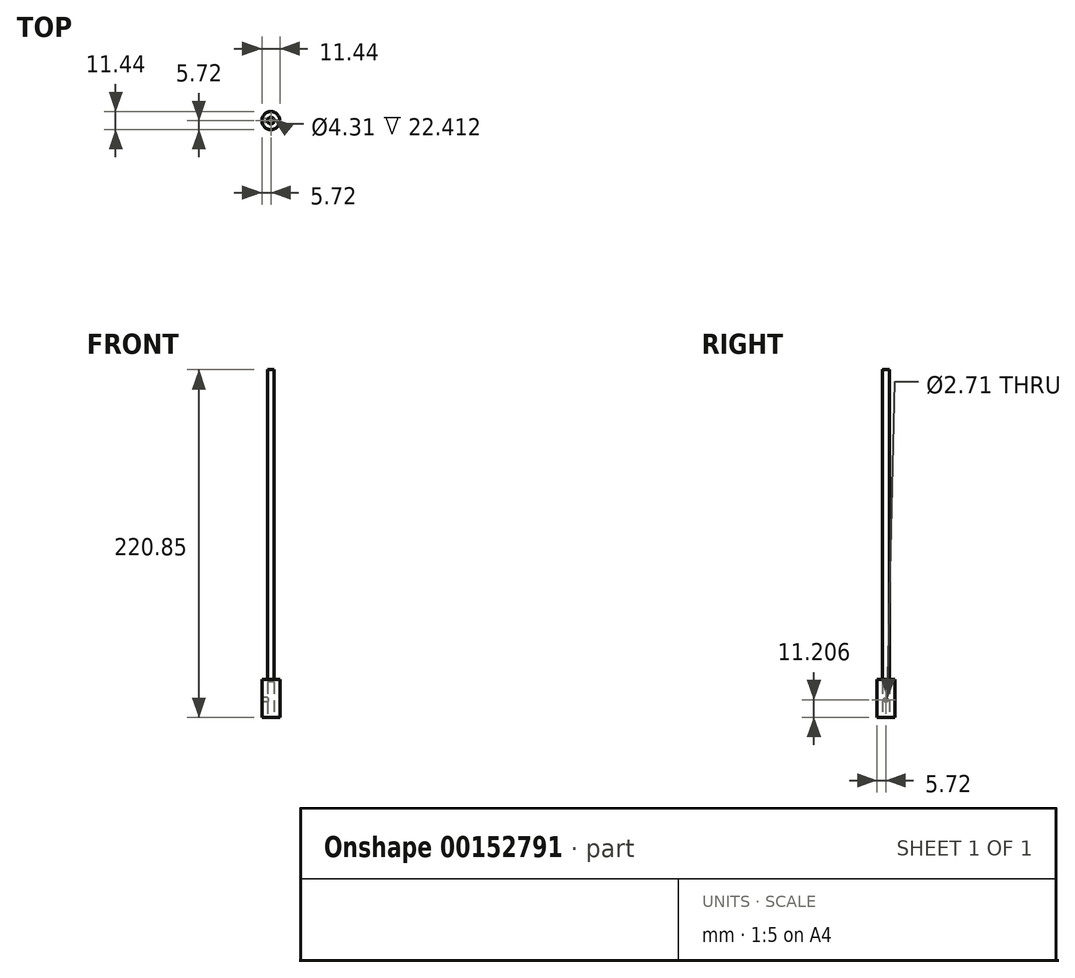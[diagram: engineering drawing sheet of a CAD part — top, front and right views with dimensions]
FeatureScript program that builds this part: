
annotation { "Feature Type Name" : "Feature", "Feature Type Description" : "" }
export const myFeature = defineFeature(function(context is Context, id is Id, definition is map)
    precondition{}
    {
        {
            var Q0;
            Q0=qCreatedBy(makeId("Top.planeOp"),FACE);
            var sketch = newSketch(context, id + "F0", { "sketchPlane" : qUnion([Q0])});
            skLineSegment(sketch, "E0.bottom", {"start": v(5.72, -5.72) * mm, "end": v(-5.72, -5.72) * mm});
            skLineSegment(sketch, "E0.top", {"start": v(5.72, 5.72) * mm, "end": v(-5.72, 5.71) * mm});
            skLineSegment(sketch, "E0.left", {"start": v(5.72, -5.72) * mm, "end": v(5.72, 5.72) * mm});
            skLineSegment(sketch, "E0.right", {"start": v(-5.72, -5.72) * mm, "end": v(-5.72, 5.71) * mm});
            skPoint(sketch, "E0.middle", {"position": v(0, 0) * mm});
            skCircle(sketch, "E1", {"center": v(0, 0) * mm, "radius": 5.72 * mm, "construction": true});
            skCircle(sketch, "E2", {"center": v(0, 0) * mm, "radius": 2.15 * mm});
            skLineSegment(sketch, "E3.bottom", {"start": v(2.15, 1.83) * mm, "end": v(5.41, 1.83) * mm, "construction": true});
            skLineSegment(sketch, "E3.top", {"start": v(2.15, -1.83) * mm, "end": v(5.41, -1.83) * mm, "construction": true});
            skLineSegment(sketch, "E3.left", {"start": v(2.15, 1.83) * mm, "end": v(2.15, -1.83) * mm, "construction": true});
            skLineSegment(sketch, "E3.right", {"start": v(5.41, 1.83) * mm, "end": v(5.41, -1.83) * mm, "construction": true});
            skLineSegment(sketch, "E4", {"start": v(2.15, 0) * mm, "end": v(0, 0) * mm, "construction": true});
            skSolve(sketch);
        }
        {
            var Q0;
            Q0=qSketchRegion(id+"F0",true);
            extrude(context, id + "F1", {"entities" : qUnion([Q0]), "depth" : 22.41 * mm});
        }
        {
            var Q0;
            Q0=makeQuery(id+"F1.opExtrude","CAP_FACE",FACE,{"disambiguationData":[OSD([sQuery(id+"F0.wireOp",EDGE,"E0.bottom"),sQuery(id+"F0.wireOp",EDGE,"E0.top"),sQuery(id+"F0.wireOp",EDGE,"E0.left"),sQuery(id+"F0.wireOp",EDGE,"E0.right"),sQuery(id+"F0.wireOp",EDGE,"E2")])],"isStart":false});
            var sketch = newSketch(context, id + "F2", { "sketchPlane" : qUnion([Q0])});
            skLineSegment(sketch, "E5.bottom", {"start": v(-5.72, 5.71) * mm, "end": v(5.72, 5.71) * mm});
            skLineSegment(sketch, "E5.top", {"start": v(-5.72, -5.71) * mm, "end": v(5.72, -5.71) * mm});
            skLineSegment(sketch, "E5.left", {"start": v(-5.72, 5.71) * mm, "end": v(-5.72, -5.71) * mm});
            skLineSegment(sketch, "E5.right", {"start": v(5.72, 5.71) * mm, "end": v(5.72, -5.71) * mm});
            skPoint(sketch, "E5.middle", {"position": v(0, 0) * mm});
            skSolve(sketch);
        }
        {
            var Q0;
            Q0=qSketchRegion(id+"F2",true);
            extrude(context, id + "F3", {"entities" : qUnion([Q0]), "operationType" : NewBodyOperationType.ADD, "depth" : 1.59 * mm});
        }
        {
            var Q0;
            Q0=makeQuery(id+"F70DsUOZgpewn3f_1.boolean.opBoolean","MERGE",FACE,{"derivedFrom":[makeQuery(id+"F3.boolean.opBoolean","MERGE",FACE,{"derivedFrom":[makeQuery(id+"F1.opExtrude","SWEPT_FACE",FACE,{"disambiguationData":[OSD([sQuery(id+"F0.wireOp",EDGE,"E0.right")])]}),makeQuery(id+"F3.opExtrude","SWEPT_FACE",FACE,{"disambiguationData":[OSD([sQuery(id+"F2.wireOp",EDGE,"E5.left")])]})]}),makeQuery(id+"F70DsUOZgpewn3f_1.opExtrude","SWEPT_FACE",FACE,{"disambiguationData":[OSD([sQuery(id+"FPdqaA84nfEKiEw_1.wireOp",EDGE,"Zp1nVK7z-LQDl-cVPR-DDhh-xMN3QgEcbA63.left")])]})]});
            var sketch = newSketch(context, id + "F4", { "sketchPlane" : qUnion([Q0])});
            skLineSegment(sketch, "E6", {"start": v(0, 0) * mm, "end": v(0, 22.41) * mm, "construction": true});
            skCircle(sketch, "E7", {"center": v(0, 11.2) * mm, "radius": 1.35 * mm});
            skSolve(sketch);
        }
        {
            var Q0;
            Q0=qSketchRegion(id+"F4",true);
            var Q1;
            Q1=makeQuery(id+"F1.opExtrude","SWEPT_FACE",FACE,{"disambiguationData":[OSD([sQuery(id+"F0.wireOp",EDGE,"E2")])]});
            extrude(context, id + "F5", {"entities" : qUnion([Q0]), "operationType" : NewBodyOperationType.REMOVE, "endBound" : BoundingType.UP_TO_SURFACE, "oppositeDirection" : true, "endBoundEntityFace" : qUnion([Q1]), "depth" : 25.4 * mm});
        }
        {
            var Q0;
            Q0=makeQuery(id+"F70DsUOZgpewn3f_1.boolean.opBoolean","MERGE",EDGE,{"derivedFrom":[makeQuery(id+"F3.boolean.opBoolean","MERGE",EDGE,{"derivedFrom":[makeQuery(id+"F1.opExtrude","SWEPT_EDGE",EDGE,{"disambiguationData":[OSD([sQuery(id+"F0.wireOp",EDGE,"E0.top"),sQuery(id+"F0.wireOp",EDGE,"E0.right")])]}),makeQuery(id+"F3.opExtrude","SWEPT_EDGE",EDGE,{"disambiguationData":[OSD([sQuery(id+"F2.wireOp",EDGE,"E5.bottom"),sQuery(id+"F2.wireOp",EDGE,"E5.left")])]})]}),makeQuery(id+"F70DsUOZgpewn3f_1.opExtrude","SWEPT_EDGE",EDGE,{"disambiguationData":[OSD([sQuery(id+"FPdqaA84nfEKiEw_1.wireOp",EDGE,"Zp1nVK7z-LQDl-cVPR-DDhh-xMN3QgEcbA63.bottom"),sQuery(id+"FPdqaA84nfEKiEw_1.wireOp",EDGE,"Zp1nVK7z-LQDl-cVPR-DDhh-xMN3QgEcbA63.left")])]})]});
            var Q1;
            Q1=makeQuery(id+"F70DsUOZgpewn3f_1.boolean.opBoolean","MERGE",EDGE,{"derivedFrom":[makeQuery(id+"F3.boolean.opBoolean","MERGE",EDGE,{"derivedFrom":[makeQuery(id+"F1.opExtrude","SWEPT_EDGE",EDGE,{"disambiguationData":[OSD([sQuery(id+"F0.wireOp",EDGE,"E0.top"),sQuery(id+"F0.wireOp",EDGE,"E0.left")])]}),makeQuery(id+"F3.opExtrude","SWEPT_EDGE",EDGE,{"disambiguationData":[OSD([sQuery(id+"F2.wireOp",EDGE,"E5.bottom"),sQuery(id+"F2.wireOp",EDGE,"E5.right")])]})]}),makeQuery(id+"F70DsUOZgpewn3f_1.opExtrude","SWEPT_EDGE",EDGE,{"disambiguationData":[OSD([sQuery(id+"FPdqaA84nfEKiEw_1.wireOp",EDGE,"Zp1nVK7z-LQDl-cVPR-DDhh-xMN3QgEcbA63.bottom"),sQuery(id+"FPdqaA84nfEKiEw_1.wireOp",EDGE,"Zp1nVK7z-LQDl-cVPR-DDhh-xMN3QgEcbA63.right")])]})]});
            var Q2;
            Q2=makeQuery(id+"F70DsUOZgpewn3f_1.boolean.opBoolean","MERGE",EDGE,{"derivedFrom":[makeQuery(id+"F3.boolean.opBoolean","MERGE",EDGE,{"derivedFrom":[makeQuery(id+"F1.opExtrude","SWEPT_EDGE",EDGE,{"disambiguationData":[OSD([sQuery(id+"F0.wireOp",EDGE,"E0.bottom"),sQuery(id+"F0.wireOp",EDGE,"E0.right")])]}),makeQuery(id+"F3.opExtrude","SWEPT_EDGE",EDGE,{"disambiguationData":[OSD([sQuery(id+"F2.wireOp",EDGE,"E5.top"),sQuery(id+"F2.wireOp",EDGE,"E5.left")])]})]}),makeQuery(id+"F70DsUOZgpewn3f_1.opExtrude","SWEPT_EDGE",EDGE,{"disambiguationData":[OSD([sQuery(id+"FPdqaA84nfEKiEw_1.wireOp",EDGE,"Zp1nVK7z-LQDl-cVPR-DDhh-xMN3QgEcbA63.top"),sQuery(id+"FPdqaA84nfEKiEw_1.wireOp",EDGE,"Zp1nVK7z-LQDl-cVPR-DDhh-xMN3QgEcbA63.left")])]})]});
            var Q3;
            Q3=makeQuery(id+"F70DsUOZgpewn3f_1.boolean.opBoolean","MERGE",EDGE,{"derivedFrom":[makeQuery(id+"F3.boolean.opBoolean","MERGE",EDGE,{"derivedFrom":[makeQuery(id+"F1.opExtrude","SWEPT_EDGE",EDGE,{"disambiguationData":[OSD([sQuery(id+"F0.wireOp",EDGE,"E0.bottom"),sQuery(id+"F0.wireOp",EDGE,"E0.left")])]}),makeQuery(id+"F3.opExtrude","SWEPT_EDGE",EDGE,{"disambiguationData":[OSD([sQuery(id+"F2.wireOp",EDGE,"E5.top"),sQuery(id+"F2.wireOp",EDGE,"E5.right")])]})]}),makeQuery(id+"F70DsUOZgpewn3f_1.opExtrude","SWEPT_EDGE",EDGE,{"disambiguationData":[OSD([sQuery(id+"FPdqaA84nfEKiEw_1.wireOp",EDGE,"Zp1nVK7z-LQDl-cVPR-DDhh-xMN3QgEcbA63.top"),sQuery(id+"FPdqaA84nfEKiEw_1.wireOp",EDGE,"Zp1nVK7z-LQDl-cVPR-DDhh-xMN3QgEcbA63.right")])]})]});
            fillet(context, id + "F6", {"entities" : qUnion([Q0, Q1, Q2, Q3]), "radius" : 5.7 * mm, "tangentPropagation" : true, "allowEdgeOverflow" : false});
        }
        {
            var Q0;
            Q0=makeQuery(id+"F3.opExtrude","CAP_FACE",FACE,{"disambiguationData":[OSD([sQuery(id+"F2.wireOp",EDGE,"E5.bottom"),sQuery(id+"F2.wireOp",EDGE,"E5.top"),sQuery(id+"F2.wireOp",EDGE,"E5.left"),sQuery(id+"F2.wireOp",EDGE,"E5.right")])],"isStart":false});
            var sketch = newSketch(context, id + "F7", { "sketchPlane" : qUnion([Q0])});
            skCircle(sketch, "E8", {"center": v(0, 0) * mm, "radius": 2.15 * mm});
            skSolve(sketch);
        }
        {
            var Q0;
            Q0=qSketchRegion(id+"F7",true);
            extrude(context, id + "F8", {"entities" : qUnion([Q0]), "operationType" : NewBodyOperationType.ADD, "depth" : 196.85 * mm});
        }
    });
